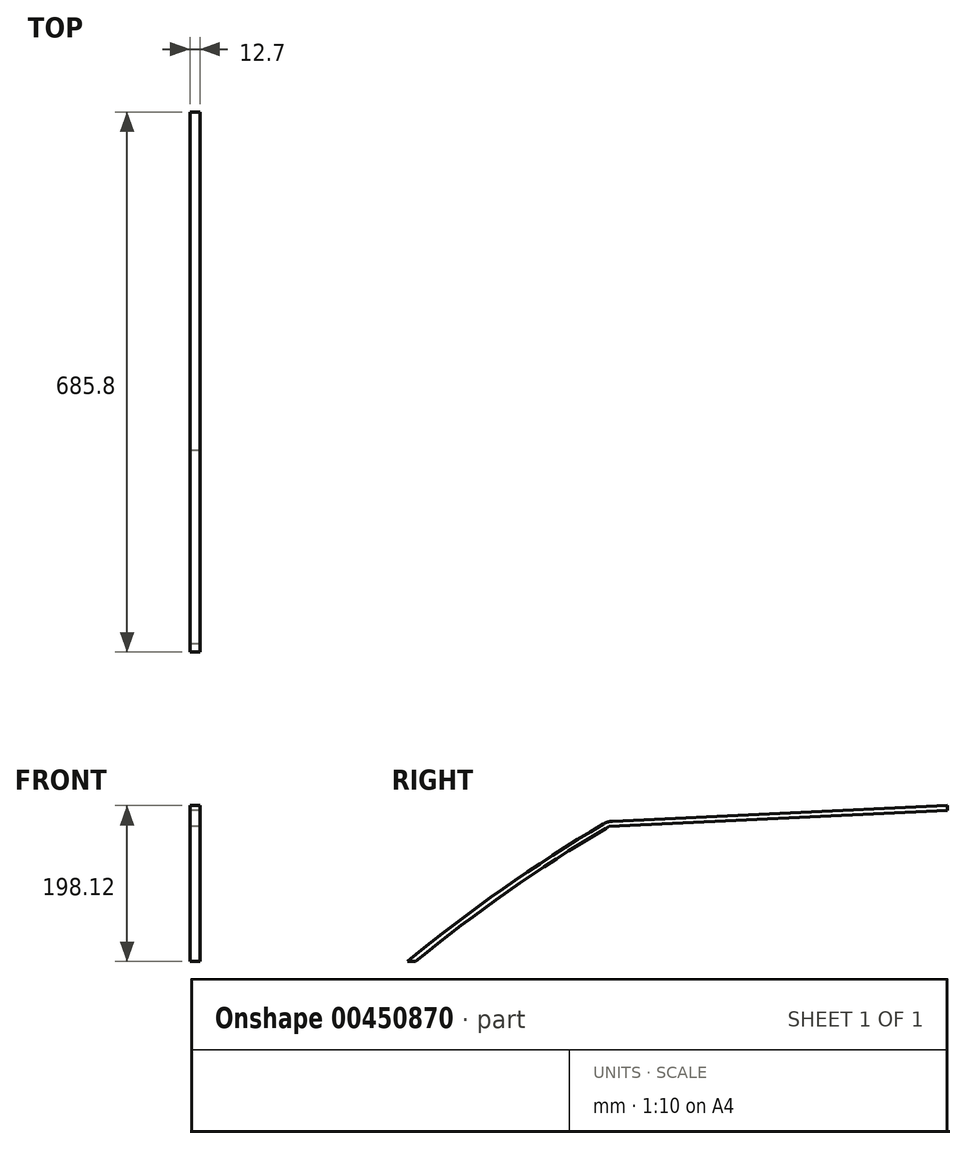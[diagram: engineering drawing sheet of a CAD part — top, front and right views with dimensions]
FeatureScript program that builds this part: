
annotation { "Feature Type Name" : "Feature", "Feature Type Description" : "" }
export const myFeature = defineFeature(function(context is Context, id is Id, definition is map)
    precondition{}
    {
        {
            var Q0;
            Q0=qCreatedBy(makeId("Right.planeOp"),FACE);
            var sketch = newSketch(context, id + "F0", { "sketchPlane" : qUnion([Q0])});
            skLineSegment(sketch, "E0", {"start": v(-329.2, 0) * mm, "end": v(-75.2, 0) * mm, "construction": true});
            skLineSegment(sketch, "E1", {"start": v(-75.2, 0) * mm, "end": v(-75.2, 177.8) * mm, "construction": true});
            skArc(sketch, "E2", {"start": v(-80.65, 174.58) * mm, "mid": v(-208.3, 92.1) * mm, "end": v(-329.2, 0) * mm});
            skLineSegment(sketch, "E3", {"start": v(-68.9, 178.1) * mm, "end": v(356.6, 198.12) * mm});
            skLineSegment(sketch, "E4", {"start": v(356.6, 198.12) * mm, "end": v(356.6, 0) * mm, "construction": true});
            skLineSegment(sketch, "E5", {"start": v(-75.2, 0) * mm, "end": v(356.6, 0) * mm, "construction": true});
            skPoint(sketch, "E6.visualSharp", {"position": v(-75.2, 177.8) * mm});
            skArc(sketch, "E6.filletArc", {"start": v(-68.9, 178.1) * mm, "mid": v(-75, 177.06) * mm, "end": v(-80.65, 174.58) * mm});
            skArc(sketch, "E7.0", {"start": v(-77.5, 169.06) * mm, "mid": v(-201.53, 89.09) * mm, "end": v(-319.19, 0) * mm});
            skLineSegment(sketch, "E8.0", {"start": v(-75, 171.45) * mm, "end": v(356.6, 191.76) * mm});
            skLineSegment(sketch, "E9", {"start": v(-329.2, 0) * mm, "end": v(-319.19, 0) * mm});
            skLineSegment(sketch, "E10", {"start": v(356.6, 198.12) * mm, "end": v(356.6, 191.76) * mm});
            skLineSegment(sketch, "E11", {"start": v(-73.34, 171.53) * mm, "end": v(-75, 171.45) * mm});
            skLineSegment(sketch, "E12", {"start": v(-77.5, 169.06) * mm, "end": v(-73.34, 171.53) * mm});
            skSolve(sketch);
        }
        {
            var Q0;
            Q0=makeQuery(id+"F0.imprint","IMPRINT",FACE,{"disambiguationData":[TD([[makeQuery(id+"F0.imprint","IMPRINT",EDGE,{"derivedFrom":sQuery(id+"F0.wireOp",EDGE,"E2")}),1.0]])]});
            extrude(context, id + "F1", {"entities" : qUnion([Q0]), "depth" : 12.7 * mm});
        }
    });
